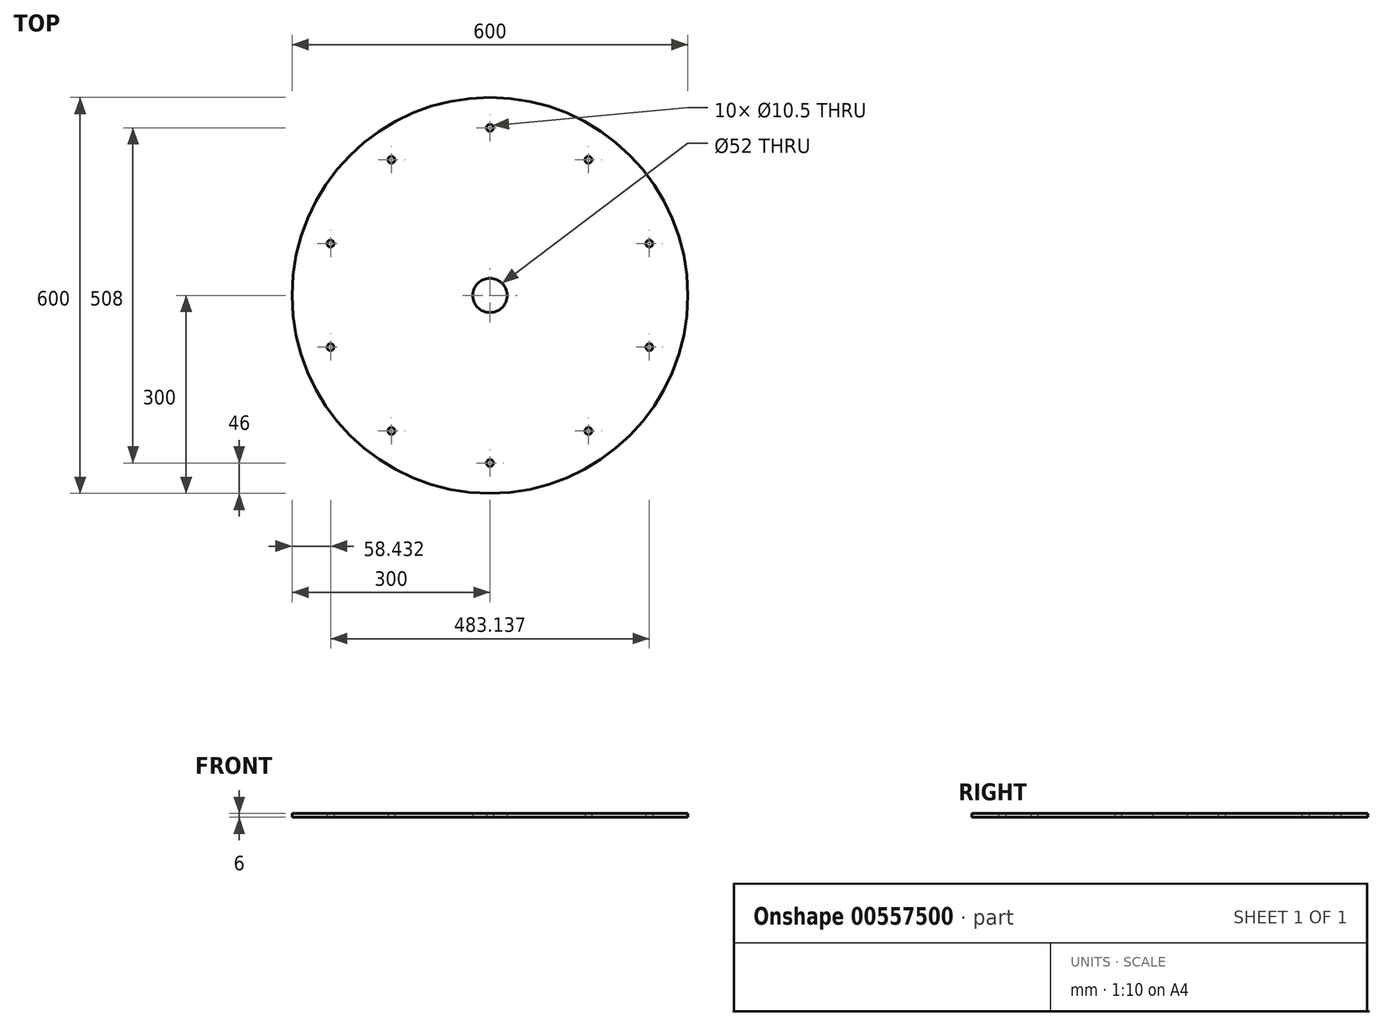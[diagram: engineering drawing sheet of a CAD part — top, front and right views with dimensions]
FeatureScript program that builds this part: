
annotation { "Feature Type Name" : "Feature", "Feature Type Description" : "" }
export const myFeature = defineFeature(function(context is Context, id is Id, definition is map)
    precondition{}
    {
        {
            var Q0;
            Q0=qCreatedBy(makeId("Top.planeOp"),FACE);
            var sketch = newSketch(context, id + "F0", { "sketchPlane" : qUnion([Q0])});
            skCircle(sketch, "E0", {"center": v(0, 0) * mm, "radius": 300 * mm});
            skCircle(sketch, "E1", {"center": v(0, 0) * mm, "radius": 26 * mm});
            skCircle(sketch, "E2", {"center": v(0, 0) * mm, "radius": 254 * mm, "construction": true});
            skCircle(sketch, "E3", {"center": v(0, 254) * mm, "radius": 5.25 * mm});
            skCircle(sketch, "E4.1.0", {"center": v(-149.3, 205.5) * mm, "radius": 5.25 * mm});
            skCircle(sketch, "E4.2.0", {"center": v(-241.57, 78.5) * mm, "radius": 5.25 * mm});
            skCircle(sketch, "E4.3.0", {"center": v(-241.57, -78.5) * mm, "radius": 5.25 * mm});
            skCircle(sketch, "E4.4.0", {"center": v(-149.3, -205.5) * mm, "radius": 5.25 * mm});
            skCircle(sketch, "E4.5.0", {"center": v(0, -254) * mm, "radius": 5.25 * mm});
            skCircle(sketch, "E4.6.0", {"center": v(149.3, -205.5) * mm, "radius": 5.25 * mm});
            skCircle(sketch, "E4.7.0", {"center": v(241.57, -78.5) * mm, "radius": 5.25 * mm});
            skCircle(sketch, "E4.8.0", {"center": v(241.57, 78.5) * mm, "radius": 5.25 * mm});
            skCircle(sketch, "E4.9.0", {"center": v(149.3, 205.5) * mm, "radius": 5.25 * mm});
            skSolve(sketch);
        }
        {
            var Q0;
            Q0=makeQuery(id+"F0.imprint","IMPRINT",FACE,{"disambiguationData":[TD([[makeQuery(id+"F0.imprint","IMPRINT",EDGE,{"derivedFrom":sQuery(id+"F0.wireOp",EDGE,"E0")}),1.0]])]});
            extrude(context, id + "F1", {"entities" : qUnion([Q0]), "depth" : 6 * mm, "offsetDistance" : 25 * mm});
        }
    });
